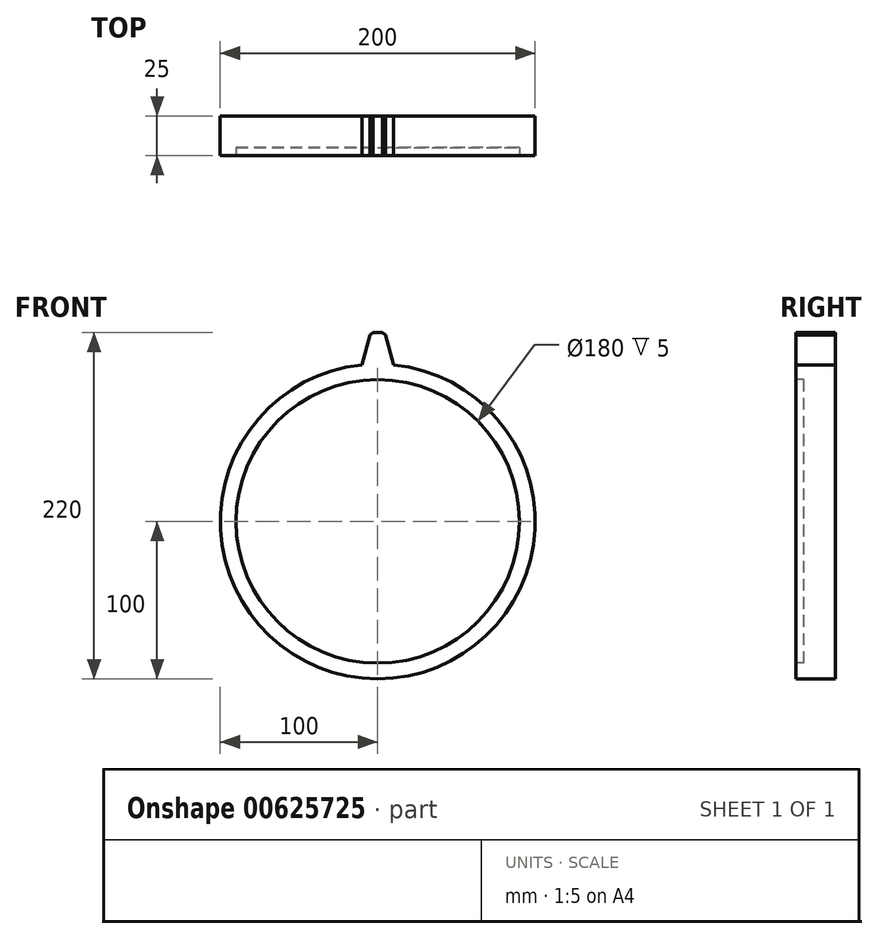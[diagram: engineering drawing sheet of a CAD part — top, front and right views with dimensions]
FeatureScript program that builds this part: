
annotation { "Feature Type Name" : "Feature", "Feature Type Description" : "" }
export const myFeature = defineFeature(function(context is Context, id is Id, definition is map)
    precondition{}
    {
        {
            var Q0;
            Q0=qCreatedBy(makeId("Front.planeOp"),FACE);
            var sketch = newSketch(context, id + "F0", { "sketchPlane" : qUnion([Q0])});
            skCircle(sketch, "E0", {"center": v(0, 0) * mm, "radius": 100 * mm});
            skSolve(sketch);
        }
        {
            var Q0;
            Q0=makeQuery(id+"F0.imprint","IMPRINT",FACE,{"disambiguationData":[TD([[makeQuery(id+"F0.imprint","IMPRINT",EDGE,{"derivedFrom":sQuery(id+"F0.wireOp",EDGE,"E0")}),1.0]])]});
            extrude(context, id + "F1", {"entities" : qUnion([Q0]), "depth" : 25 * mm, "offsetDistance" : 25 * mm});
        }
        {
            var Q0;
            Q0=qCreatedBy(makeId("Front.planeOp"),FACE);
            var sketch = newSketch(context, id + "F2", { "sketchPlane" : qUnion([Q0])});
            skLineSegment(sketch, "E1", {"start": v(-4.5, 120) * mm, "end": v(4.5, 120) * mm});
            skLineSegment(sketch, "E2", {"start": v(4.5, 120) * mm, "end": v(10, 99.5) * mm});
            skLineSegment(sketch, "E3", {"start": v(10, 99.5) * mm, "end": v(-10, 99.5) * mm});
            skLineSegment(sketch, "E4", {"start": v(-10, 99.5) * mm, "end": v(-4.5, 120) * mm});
            skSolve(sketch);
        }
        {
            var Q0;
            Q0=makeQuery(id+"F2.imprint","IMPRINT",FACE,{"disambiguationData":[TD([[makeQuery(id+"F2.imprint","IMPRINT",EDGE,{"derivedFrom":sQuery(id+"F2.wireOp",EDGE,"E1")}),-1.0]])]});
            extrude(context, id + "F3", {"entities" : qUnion([Q0]), "operationType" : NewBodyOperationType.ADD, "depth" : 25 * mm, "offsetDistance" : 25 * mm});
        }
        {
            var Q0;
            Q0=makeQuery(id+"F3.opExtrude","SWEPT_EDGE",EDGE,{"disambiguationData":[OSD([sQuery(id+"F2.wireOp",EDGE,"E1"),sQuery(id+"F2.wireOp",EDGE,"E2")])]});
            var Q1;
            Q1=makeQuery(id+"F3.opExtrude","SWEPT_EDGE",EDGE,{"disambiguationData":[OSD([sQuery(id+"F2.wireOp",EDGE,"E1"),sQuery(id+"F2.wireOp",EDGE,"E4")])]});
            chamfer(context, id + "F4", {"entities" : qUnion([Q0, Q1]), "width" : 2 * mm, "tangentPropagation" : true});
        }
        {
            var Q0;
            Q0=makeQuery(id+"F3.opExtrude","SWEPT_EDGE",EDGE,{"disambiguationData":[OSD([sQuery(id+"F2.wireOp",EDGE,"E2"),sQuery(id+"F2.wireOp",EDGE,"E3")])]});
            var Q1;
            Q1=makeQuery(id+"F3.opExtrude","SWEPT_EDGE",EDGE,{"disambiguationData":[OSD([sQuery(id+"F2.wireOp",EDGE,"E3"),sQuery(id+"F2.wireOp",EDGE,"E4")])]});
            fillet(context, id + "F5", {"entities" : qUnion([Q0, Q1]), "radius" : 5 * mm, "tangentPropagation" : true, "allowEdgeOverflow" : false});
        }
        {
            var Q0;
            {var subQ0=sQuery(id+"F2.wireOp",EDGE,"E4");var subQ1=sQuery(id+"F2.wireOp",EDGE,"E3");var subQ2=sQuery(id+"F2.wireOp",EDGE,"E2");var subQ3=sQuery(id+"F2.wireOp",EDGE,"E1");Q0=makeQuery(id+"FmFrbvynnwdKjcF_1.19.F3.boolean.opBoolean","MERGE",FACE,{"derivedFrom":[makeQuery(id+"FmFrbvynnwdKjcF_1.18.F3.boolean.opBoolean","MERGE",FACE,{"derivedFrom":[makeQuery(id+"FmFrbvynnwdKjcF_1.17.F3.boolean.opBoolean","MERGE",FACE,{"derivedFrom":[makeQuery(id+"FmFrbvynnwdKjcF_1.16.F3.boolean.opBoolean","MERGE",FACE,{"derivedFrom":[makeQuery(id+"FmFrbvynnwdKjcF_1.15.F3.boolean.opBoolean","MERGE",FACE,{"derivedFrom":[makeQuery(id+"FmFrbvynnwdKjcF_1.14.F3.boolean.opBoolean","MERGE",FACE,{"derivedFrom":[makeQuery(id+"FmFrbvynnwdKjcF_1.13.F3.boolean.opBoolean","MERGE",FACE,{"derivedFrom":[makeQuery(id+"FmFrbvynnwdKjcF_1.12.F3.boolean.opBoolean","MERGE",FACE,{"derivedFrom":[makeQuery(id+"FmFrbvynnwdKjcF_1.11.F3.boolean.opBoolean","MERGE",FACE,{"derivedFrom":[makeQuery(id+"FmFrbvynnwdKjcF_1.10.F3.boolean.opBoolean","MERGE",FACE,{"derivedFrom":[makeQuery(id+"FmFrbvynnwdKjcF_1.9.F3.boolean.opBoolean","MERGE",FACE,{"derivedFrom":[makeQuery(id+"FmFrbvynnwdKjcF_1.8.F3.boolean.opBoolean","MERGE",FACE,{"derivedFrom":[makeQuery(id+"FmFrbvynnwdKjcF_1.7.F3.boolean.opBoolean","MERGE",FACE,{"derivedFrom":[makeQuery(id+"FmFrbvynnwdKjcF_1.6.F3.boolean.opBoolean","MERGE",FACE,{"derivedFrom":[makeQuery(id+"FmFrbvynnwdKjcF_1.5.F3.boolean.opBoolean","MERGE",FACE,{"derivedFrom":[makeQuery(id+"FmFrbvynnwdKjcF_1.4.F3.boolean.opBoolean","MERGE",FACE,{"derivedFrom":[makeQuery(id+"FmFrbvynnwdKjcF_1.3.F3.boolean.opBoolean","MERGE",FACE,{"derivedFrom":[makeQuery(id+"FmFrbvynnwdKjcF_1.2.F3.boolean.opBoolean","MERGE",FACE,{"derivedFrom":[makeQuery(id+"FmFrbvynnwdKjcF_1.1.F3.boolean.opBoolean","MERGE",FACE,{"derivedFrom":[makeQuery(id+"F3.boolean.opBoolean","MERGE",FACE,{"derivedFrom":[makeQuery(id+"F1.opExtrude","CAP_FACE",FACE,{"disambiguationData":[OSD([sQuery(id+"F0.wireOp",EDGE,"E0")])],"isStart":false}),makeQuery(id+"F3.opExtrude","CAP_FACE",FACE,{"disambiguationData":[OSD([subQ3,subQ2,subQ1,subQ0])],"isStart":false})]}),makeQuery(id+"FmFrbvynnwdKjcF_1.1.F3.opExtrude","CAP_FACE",FACE,{"disambiguationData":[OSD([subQ3,subQ2,subQ1,subQ0])],"isStart":false})]}),makeQuery(id+"FmFrbvynnwdKjcF_1.2.F3.opExtrude","CAP_FACE",FACE,{"disambiguationData":[OSD([subQ3,subQ2,subQ1,subQ0])],"isStart":false})]}),makeQuery(id+"FmFrbvynnwdKjcF_1.3.F3.opExtrude","CAP_FACE",FACE,{"disambiguationData":[OSD([subQ3,subQ2,subQ1,subQ0])],"isStart":false})]}),makeQuery(id+"FmFrbvynnwdKjcF_1.4.F3.opExtrude","CAP_FACE",FACE,{"disambiguationData":[OSD([subQ3,subQ2,subQ1,subQ0])],"isStart":false})]}),makeQuery(id+"FmFrbvynnwdKjcF_1.5.F3.opExtrude","CAP_FACE",FACE,{"disambiguationData":[OSD([subQ3,subQ2,subQ1,subQ0])],"isStart":false})]}),makeQuery(id+"FmFrbvynnwdKjcF_1.6.F3.opExtrude","CAP_FACE",FACE,{"disambiguationData":[OSD([subQ3,subQ2,subQ1,subQ0])],"isStart":false})]}),makeQuery(id+"FmFrbvynnwdKjcF_1.7.F3.opExtrude","CAP_FACE",FACE,{"disambiguationData":[OSD([subQ3,subQ2,subQ1,subQ0])],"isStart":false})]}),makeQuery(id+"FmFrbvynnwdKjcF_1.8.F3.opExtrude","CAP_FACE",FACE,{"disambiguationData":[OSD([subQ3,subQ2,subQ1,subQ0])],"isStart":false})]}),makeQuery(id+"FmFrbvynnwdKjcF_1.9.F3.opExtrude","CAP_FACE",FACE,{"disambiguationData":[OSD([subQ3,subQ2,subQ1,subQ0])],"isStart":false})]}),makeQuery(id+"FmFrbvynnwdKjcF_1.10.F3.opExtrude","CAP_FACE",FACE,{"disambiguationData":[OSD([subQ3,subQ2,subQ1,subQ0])],"isStart":false})]}),makeQuery(id+"FmFrbvynnwdKjcF_1.11.F3.opExtrude","CAP_FACE",FACE,{"disambiguationData":[OSD([subQ3,subQ2,subQ1,subQ0])],"isStart":false})]}),makeQuery(id+"FmFrbvynnwdKjcF_1.12.F3.opExtrude","CAP_FACE",FACE,{"disambiguationData":[OSD([subQ3,subQ2,subQ1,subQ0])],"isStart":false})]}),makeQuery(id+"FmFrbvynnwdKjcF_1.13.F3.opExtrude","CAP_FACE",FACE,{"disambiguationData":[OSD([subQ3,subQ2,subQ1,subQ0])],"isStart":false})]}),makeQuery(id+"FmFrbvynnwdKjcF_1.14.F3.opExtrude","CAP_FACE",FACE,{"disambiguationData":[OSD([subQ3,subQ2,subQ1,subQ0])],"isStart":false})]}),makeQuery(id+"FmFrbvynnwdKjcF_1.15.F3.opExtrude","CAP_FACE",FACE,{"disambiguationData":[OSD([subQ3,subQ2,subQ1,subQ0])],"isStart":false})]}),makeQuery(id+"FmFrbvynnwdKjcF_1.16.F3.opExtrude","CAP_FACE",FACE,{"disambiguationData":[OSD([subQ3,subQ2,subQ1,subQ0])],"isStart":false})]}),makeQuery(id+"FmFrbvynnwdKjcF_1.17.F3.opExtrude","CAP_FACE",FACE,{"disambiguationData":[OSD([subQ3,subQ2,subQ1,subQ0])],"isStart":false})]}),makeQuery(id+"FmFrbvynnwdKjcF_1.18.F3.opExtrude","CAP_FACE",FACE,{"disambiguationData":[OSD([subQ3,subQ2,subQ1,subQ0])],"isStart":false})]}),makeQuery(id+"FmFrbvynnwdKjcF_1.19.F3.opExtrude","CAP_FACE",FACE,{"disambiguationData":[OSD([subQ3,subQ2,subQ1,subQ0])],"isStart":false})]});}
            var sketch = newSketch(context, id + "F6", { "sketchPlane" : qUnion([Q0])});
            skCircle(sketch, "E5", {"center": v(0, 0) * mm, "radius": 90 * mm});
            skSolve(sketch);
        }
        {
            var Q0;
            Q0=makeQuery(id+"F6.imprint","IMPRINT",FACE,{"disambiguationData":[TD([[makeQuery(id+"F6.imprint","IMPRINT",EDGE,{"derivedFrom":sQuery(id+"F6.wireOp",EDGE,"E5")}),1.0]])]});
            extrude(context, id + "F7", {"entities" : qUnion([Q0]), "operationType" : NewBodyOperationType.REMOVE, "oppositeDirection" : true, "depth" : 5 * mm, "offsetDistance" : 25 * mm});
        }
    });
